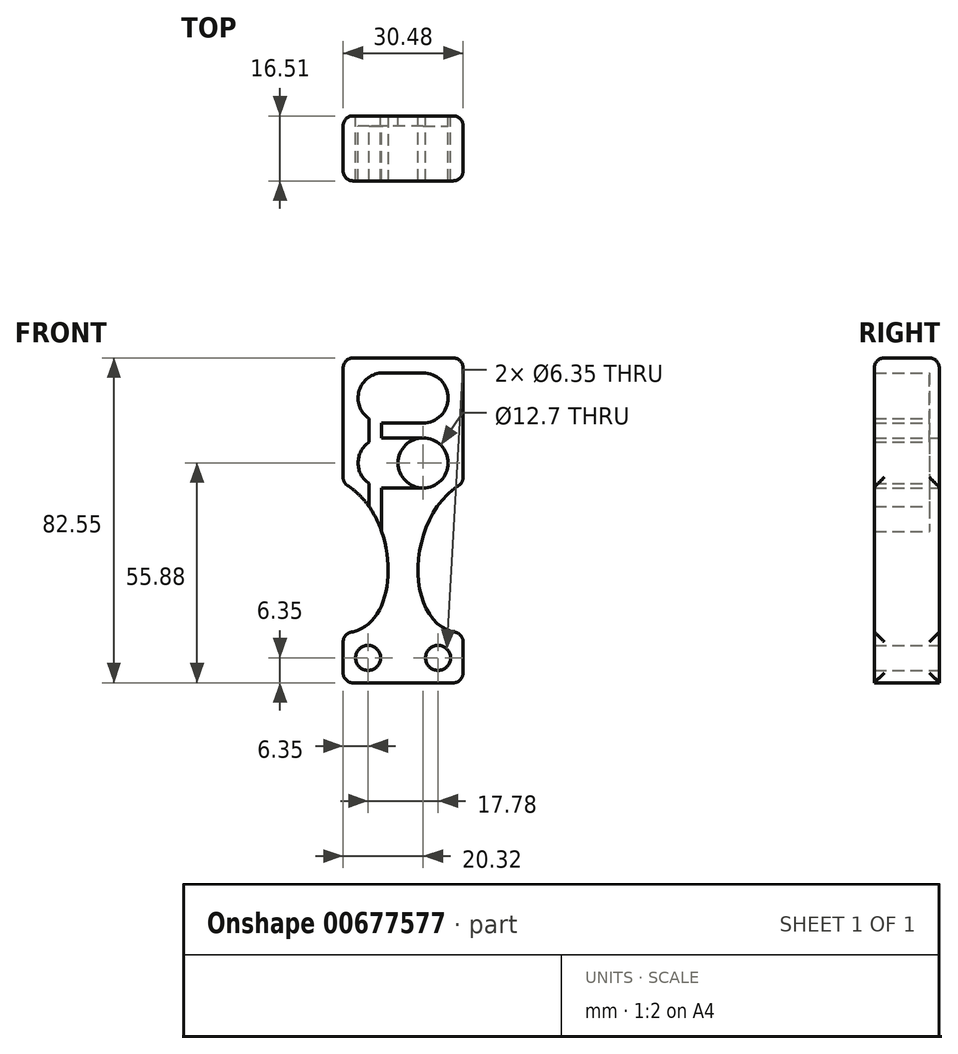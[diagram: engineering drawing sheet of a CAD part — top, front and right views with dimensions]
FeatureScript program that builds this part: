
annotation { "Feature Type Name" : "Feature", "Feature Type Description" : "" }
export const myFeature = defineFeature(function(context is Context, id is Id, definition is map)
    precondition{}
    {
        {
            var Q0;
            Q0=qCreatedBy(makeId("Front.planeOp"),FACE);
            var sketch = newSketch(context, id + "F0", { "sketchPlane" : qUnion([Q0])});
            skLineSegment(sketch, "E0", {"start": v(0, 10.16) * mm, "end": v(15.24, 10.16) * mm});
            skLineSegment(sketch, "E1", {"start": v(15.24, 10.16) * mm, "end": v(15.24, -21.59) * mm});
            skLineSegment(sketch, "E2.MirrorCS", {"start": v(-15.24, 10.16) * mm, "end": v(-15.24, -21.59) * mm});
            skLineSegment(sketch, "E3.MirrorCS", {"start": v(0, 10.16) * mm, "end": v(-15.24, 10.16) * mm});
            skCircle(sketch, "E4", {"center": v(5.08, 0) * mm, "radius": 6.35 * mm});
            skCircle(sketch, "E5.MirrorC", {"center": v(-5.08, 0) * mm, "radius": 6.35 * mm});
            skLineSegment(sketch, "E6", {"start": v(5.08, 6.35) * mm, "end": v(-5.08, 6.35) * mm});
            skLineSegment(sketch, "E7", {"start": v(-5.08, -6.35) * mm, "end": v(5.08, -6.35) * mm});
            skFitSpline(sketch, "E8", {"points": [v(-15.24, -21.59) * mm, v(-15.24, -59.7) * mm], "startDerivative": vector(45.72, -24.57) * mm, "endDerivative": vector(-45.72, 0.3) * mm});
            skFitSpline(sketch, "E9.MirrorCS", {"points": [v(15.24, -21.59) * mm, v(15.24, -59.69) * mm], "startDerivative": vector(-45.72, -24.57) * mm, "endDerivative": vector(45.72, 0.3) * mm});
            skCircle(sketch, "E10", {"center": v(-5.08, -16.51) * mm, "radius": 6.35 * mm});
            skCircle(sketch, "E11.MirrorC", {"center": v(5.08, -16.51) * mm, "radius": 6.35 * mm});
            skLineSegment(sketch, "E12", {"start": v(5.08, -10.16) * mm, "end": v(-5.08, -10.16) * mm});
            skLineSegment(sketch, "E13", {"start": v(5.08, -22.86) * mm, "end": v(-5.08, -22.86) * mm});
            skPoint(sketch, "E14", {"position": v(0, -16.51) * mm});
            skLineSegment(sketch, "E15", {"start": v(-8.64, -21.77) * mm, "end": v(-8.64, -27.62) * mm});
            skLineSegment(sketch, "E16", {"start": v(-5.46, -6.34) * mm, "end": v(-5.46, -10.17) * mm});
            skLineSegment(sketch, "E17", {"start": v(-5.46, -10.17) * mm, "end": v(-5.46, -22.6) * mm});
            skLineSegment(sketch, "E18", {"start": v(-5.46, -22.6) * mm, "end": v(-5.46, -33.95) * mm});
            skLineSegment(sketch, "E19", {"start": v(-15.24, -59.7) * mm, "end": v(-15.24, -72.39) * mm});
            skLineSegment(sketch, "E20", {"start": v(15.24, -59.69) * mm, "end": v(15.24, -72.39) * mm});
            skLineSegment(sketch, "E21", {"start": v(-8.64, -11.25) * mm, "end": v(-8.64, -5.26) * mm});
            skCircle(sketch, "E22", {"center": v(8.89, -66.04) * mm, "radius": 3.18 * mm});
            skCircle(sketch, "E23.MirrorC", {"center": v(-8.89, -66.04) * mm, "radius": 3.18 * mm});
            skLineSegment(sketch, "E24", {"start": v(-15.24, -72.39) * mm, "end": v(15.24, -72.39) * mm});
            skPoint(sketch, "E25", {"position": v(-15.24, -66.04) * mm});
            skSolve(sketch);
        }
        {
            var Q0;
            Q0=makeQuery(id+"F0.imprint","IMPRINT",FACE,{"disambiguationData":[TD([[makeQuery(id+"F0.imprint","IMPRINT",EDGE,{"derivedFrom":sQuery(id+"F0.wireOp",EDGE,"E0")}),-1.0]])]});
            extrude(context, id + "F1", {"entities" : qUnion([Q0]), "depth" : 16.5 * mm, "offsetDistance" : 25.4 * mm});
        }
        {
            var Q0;
            {var subQ0=sQuery(id+"F0.wireOp",EDGE,"E5.MirrorC");var subQ2=sQuery(id+"F0.wireOp",EDGE,"E4");var subQ5=makeQuery(id+"F0.imprint","INTERSECT",VERTEX,{"disambiguationData":[OD(0.0)],"derivedFrom":[subQ2,subQ0]});Q0=makeQuery(id+"F0.imprint","IMPRINT",FACE,{"disambiguationData":[TD([[makeQuery(id+"F0.imprint","IMPRINT",EDGE,{"disambiguationData":[TD([[subQ5,-1.0]])],"derivedFrom":subQ2}),-1.0]])]});}
            var Q1;
            {var subQ0=sQuery(id+"F0.wireOp",EDGE,"E4");var subQ1=makeQuery(id+"F0.imprint","INTERSECT",VERTEX,{"derivedFrom":[subQ0,sQuery(id+"F0.wireOp",EDGE,"E6")]});Q1=makeQuery(id+"F0.imprint","IMPRINT",FACE,{"disambiguationData":[TD([[makeQuery(id+"F0.imprint","IMPRINT",EDGE,{"disambiguationData":[TD([[subQ1,-1.0]])],"derivedFrom":subQ0}),1.0]])]});}
            var Q2;
            {var subQ0=sQuery(id+"F0.wireOp",EDGE,"E6");Q2=makeQuery(id+"F0.imprint","IMPRINT",FACE,{"disambiguationData":[TD([[makeQuery(id+"F0.imprint","IMPRINT",EDGE,{"derivedFrom":subQ0}),1.0]])]});}
            var Q3;
            {var subQ0=sQuery(id+"F0.wireOp",EDGE,"E5.MirrorC");var subQ1=sQuery(id+"F0.wireOp",EDGE,"E4");var subQ2=makeQuery(id+"F0.imprint","INTERSECT",VERTEX,{"disambiguationData":[OD(0.0)],"derivedFrom":[subQ1,subQ0]});Q3=makeQuery(id+"F0.imprint","IMPRINT",FACE,{"disambiguationData":[TD([[makeQuery(id+"F0.imprint","IMPRINT",EDGE,{"disambiguationData":[TD([[subQ2,-1.0]])],"derivedFrom":subQ1}),1.0]])]});}
            var Q4;
            {var subQ0=sQuery(id+"F0.wireOp",EDGE,"E7");Q4=makeQuery(id+"F0.imprint","IMPRINT",FACE,{"disambiguationData":[TD([[makeQuery(id+"F0.imprint","IMPRINT",EDGE,{"derivedFrom":subQ0}),1.0]])]});}
            var Q5;
            {var subQ0=sQuery(id+"F0.wireOp",EDGE,"E10");var subQ4=makeQuery(id+"F0.imprint","INTERSECT",VERTEX,{"derivedFrom":[subQ0,sQuery(id+"F0.wireOp",EDGE,"E12")]});Q5=makeQuery(id+"F0.imprint","IMPRINT",FACE,{"disambiguationData":[TD([[makeQuery(id+"F0.imprint","IMPRINT",EDGE,{"disambiguationData":[TD([[subQ4,1.0]])],"derivedFrom":subQ0}),1.0]])]});}
            var Q6;
            {var subQ0=sQuery(id+"F0.wireOp",EDGE,"E10");var subQ2=sQuery(id+"F0.wireOp",EDGE,"E17");var subQ4=makeQuery(id+"F0.imprint","INTERSECT",VERTEX,{"derivedFrom":[subQ0,subQ2]});Q6=makeQuery(id+"F0.imprint","IMPRINT",FACE,{"disambiguationData":[TD([[makeQuery(id+"F0.imprint","IMPRINT",EDGE,{"disambiguationData":[TD([[subQ4,1.0]])],"derivedFrom":subQ0}),1.0]])]});}
            var Q7;
            {var subQ0=sQuery(id+"F0.wireOp",EDGE,"E11.MirrorC");var subQ1=sQuery(id+"F0.wireOp",EDGE,"E10");var subQ2=makeQuery(id+"F0.imprint","INTERSECT",VERTEX,{"disambiguationData":[OD(0.0)],"derivedFrom":[subQ1,subQ0]});Q7=makeQuery(id+"F0.imprint","IMPRINT",FACE,{"disambiguationData":[TD([[makeQuery(id+"F0.imprint","IMPRINT",EDGE,{"disambiguationData":[TD([[subQ2,1.0]])],"derivedFrom":subQ1}),1.0]])]});}
            var Q8;
            {var subQ0=sQuery(id+"F0.wireOp",EDGE,"E12");Q8=makeQuery(id+"F0.imprint","IMPRINT",FACE,{"disambiguationData":[TD([[makeQuery(id+"F0.imprint","IMPRINT",EDGE,{"derivedFrom":subQ0}),1.0]])]});}
            var Q9;
            {var subQ0=sQuery(id+"F0.wireOp",EDGE,"E11.MirrorC");var subQ1=sQuery(id+"F0.wireOp",EDGE,"E10");var subQ2=makeQuery(id+"F0.imprint","INTERSECT",VERTEX,{"disambiguationData":[OD(0.0)],"derivedFrom":[subQ1,subQ0]});Q9=makeQuery(id+"F0.imprint","IMPRINT",FACE,{"disambiguationData":[TD([[makeQuery(id+"F0.imprint","IMPRINT",EDGE,{"disambiguationData":[TD([[subQ2,1.0]])],"derivedFrom":subQ1}),-1.0]])]});}
            var Q10;
            {var subQ0=sQuery(id+"F0.wireOp",EDGE,"E13");Q10=makeQuery(id+"F0.imprint","IMPRINT",FACE,{"disambiguationData":[TD([[makeQuery(id+"F0.imprint","IMPRINT",EDGE,{"derivedFrom":subQ0}),-1.0]])]});}
            var Q11;
            {var subQ0=sQuery(id+"F0.wireOp",EDGE,"3nQBnrxE-CDFu-dkHD-LFef-8Zr9rkai0jz6");Q11=makeQuery(id+"F0.imprint","IMPRINT",FACE,{"disambiguationData":[TD([[makeQuery(id+"F0.imprint","IMPRINT",EDGE,{"derivedFrom":subQ0}),1.0]])]});}
            var Q12;
            {var subQ0=sQuery(id+"F0.wireOp",EDGE,"E15");Q12=makeQuery(id+"F0.imprint","IMPRINT",FACE,{"disambiguationData":[TD([[makeQuery(id+"F0.imprint","IMPRINT",EDGE,{"derivedFrom":subQ0}),1.0]])]});}
            var Q13;
            {var subQ0=sQuery(id+"F0.wireOp",EDGE,"E16");Q13=makeQuery(id+"F0.imprint","IMPRINT",FACE,{"disambiguationData":[TD([[makeQuery(id+"F0.imprint","IMPRINT",EDGE,{"derivedFrom":subQ0}),-1.0]])]});}
            var Q14;
            {var subQ0=sQuery(id+"F0.wireOp",EDGE,"E17");Q14=makeQuery(id+"F0.imprint","IMPRINT",FACE,{"disambiguationData":[TD([[makeQuery(id+"F0.imprint","IMPRINT",EDGE,{"derivedFrom":subQ0}),-1.0]])]});}
            extrude(context, id + "F2", {"entities" : qUnion([Q0, Q1, Q2, Q3, Q4, Q5, Q6, Q7, Q8, Q9, Q10, Q11, Q12, Q13, Q14]), "operationType" : NewBodyOperationType.ADD, "depth" : 2.54 * mm, "offsetDistance" : 25.4 * mm});
        }
        {
            var Q0;
            Q0=makeQuery(id+"F1.opExtrude","SWEPT_FACE",FACE,{"disambiguationData":[OSD([sQuery(id+"F0.wireOp",EDGE,"E0"),sQuery(id+"F0.wireOp",EDGE,"E3.MirrorCS")])]});
            var Q1;
            Q1=makeQuery(id+"F1.opExtrude","SWEPT_FACE",FACE,{"disambiguationData":[OSD([sQuery(id+"F0.wireOp",EDGE,"E1")])]});
            var Q2;
            Q2=makeQuery(id+"F1.opExtrude","SWEPT_FACE",FACE,{"disambiguationData":[OSD([sQuery(id+"F0.wireOp",EDGE,"E2.MirrorCS")])]});
            var Q3;
            Q3=makeQuery(id+"F1.opExtrude","SWEPT_FACE",FACE,{"disambiguationData":[OSD([sQuery(id+"F0.wireOp",EDGE,"E20")])]});
            var Q4;
            Q4=makeQuery(id+"F1.opExtrude","SWEPT_FACE",FACE,{"disambiguationData":[OSD([sQuery(id+"F0.wireOp",EDGE,"E19")])]});
            fillet(context, id + "F3", {"entities" : qUnion([Q0, Q1, Q2, Q3, Q4]), "radius" : 2.54 * mm, "tangentPropagation" : true, "allowEdgeOverflow" : false});
        }
    });
